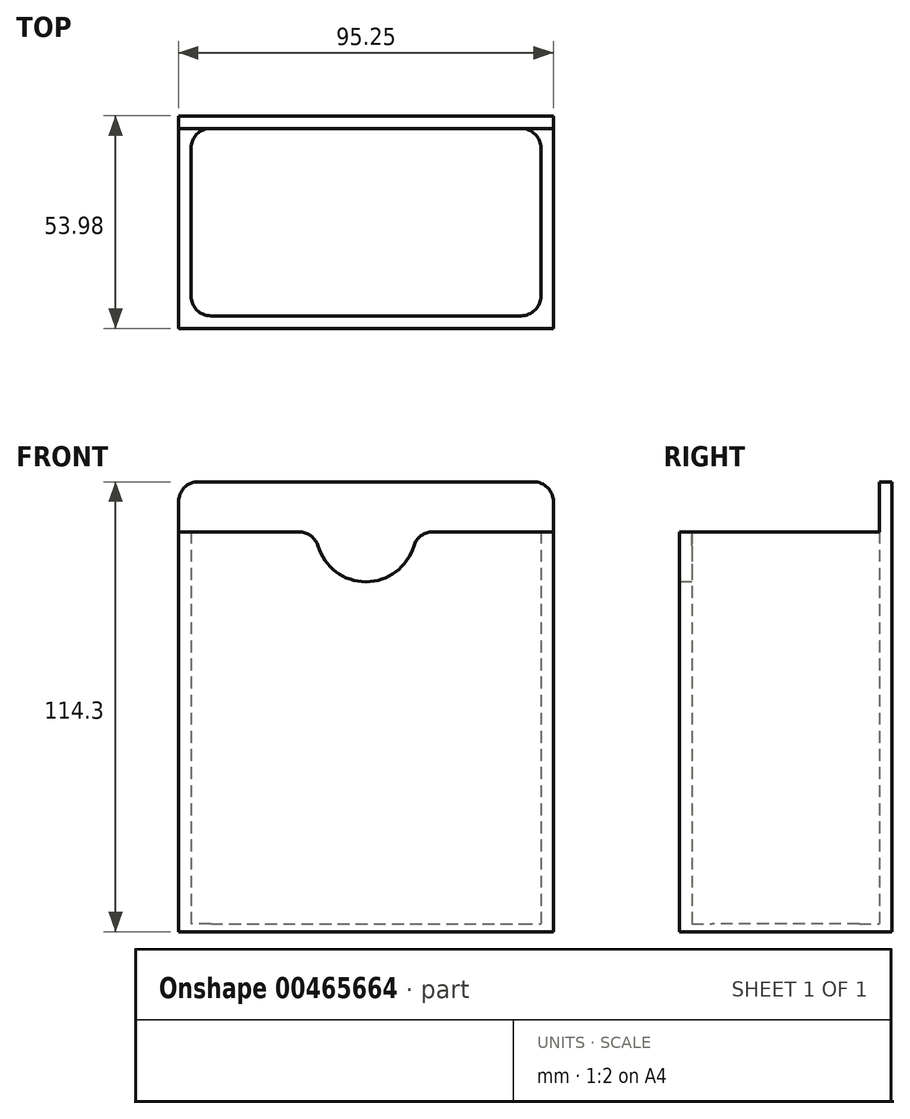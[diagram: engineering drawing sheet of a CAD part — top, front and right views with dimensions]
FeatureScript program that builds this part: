
annotation { "Feature Type Name" : "Feature", "Feature Type Description" : "" }
export const myFeature = defineFeature(function(context is Context, id is Id, definition is map)
    precondition{}
    {
        {
            var Q0;
            Q0=qCreatedBy(makeId("Top.planeOp"),FACE);
            var sketch = newSketch(context, id + "F0", { "sketchPlane" : qUnion([Q0])});
            skLineSegment(sketch, "E0.bottom", {"start": v(0, 0) * mm, "end": v(95.25, 0) * mm});
            skLineSegment(sketch, "E0.top", {"start": v(0, 53.98) * mm, "end": v(95.25, 53.98) * mm});
            skLineSegment(sketch, "E0.left", {"start": v(0, 0) * mm, "end": v(0, 53.98) * mm});
            skLineSegment(sketch, "E0.right", {"start": v(95.25, 0) * mm, "end": v(95.25, 53.98) * mm});
            skSolve(sketch);
        }
        {
            var Q0;
            Q0=qSketchRegion(id+"F0",true);
            extrude(context, id + "F1", {"entities" : qUnion([Q0]), "depth" : 2.03 * mm});
        }
        {
            var Q0;
            Q0=makeQuery(id+"F1.opExtrude","CAP_FACE",FACE,{"disambiguationData":[OSD([sQuery(id+"F0.wireOp",EDGE,"E0.bottom"),sQuery(id+"F0.wireOp",EDGE,"E0.top"),sQuery(id+"F0.wireOp",EDGE,"E0.left"),sQuery(id+"F0.wireOp",EDGE,"E0.right")])],"isStart":false});
            var sketch = newSketch(context, id + "F2", { "sketchPlane" : qUnion([Q0])});
            skLineSegment(sketch, "E1.bottom", {"start": v(0, 53.98) * mm, "end": v(95.25, 53.98) * mm});
            skLineSegment(sketch, "E1.top", {"start": v(0, 0) * mm, "end": v(95.25, 0) * mm});
            skLineSegment(sketch, "E1.left", {"start": v(0, 53.98) * mm, "end": v(0, 0) * mm});
            skLineSegment(sketch, "E1.right", {"start": v(95.25, 53.98) * mm, "end": v(95.25, 0) * mm});
            skLineSegment(sketch, "E2.0", {"start": v(3.18, 50.8) * mm, "end": v(3.18, 3.18) * mm});
            skLineSegment(sketch, "E2.1", {"start": v(3.18, 50.8) * mm, "end": v(92.08, 50.8) * mm});
            skLineSegment(sketch, "E2.2", {"start": v(92.08, 50.8) * mm, "end": v(92.08, 3.18) * mm});
            skLineSegment(sketch, "E2.3", {"start": v(3.18, 3.18) * mm, "end": v(92.08, 3.18) * mm});
            skSolve(sketch);
        }
        {
            var Q0;
            Q0=qSketchRegion(id+"F2",true);
            extrude(context, id + "F3", {"entities" : qUnion([Q0]), "operationType" : NewBodyOperationType.ADD, "depth" : 99.57 * mm});
        }
        {
            var Q0;
            Q0=makeQuery(id+"F3.opExtrude","CAP_FACE",FACE,{"disambiguationData":[OSD([sQuery(id+"F2.wireOp",EDGE,"E1.bottom"),sQuery(id+"F2.wireOp",EDGE,"E1.top"),sQuery(id+"F2.wireOp",EDGE,"E1.left"),sQuery(id+"F2.wireOp",EDGE,"E1.right"),sQuery(id+"F2.wireOp",EDGE,"E2.0"),sQuery(id+"F2.wireOp",EDGE,"E2.1"),sQuery(id+"F2.wireOp",EDGE,"E2.2"),sQuery(id+"F2.wireOp",EDGE,"E2.3")])],"isStart":false});
            var sketch = newSketch(context, id + "F4", { "sketchPlane" : qUnion([Q0])});
            skLineSegment(sketch, "E3.bottom", {"start": v(0, 53.98) * mm, "end": v(95.25, 53.98) * mm});
            skLineSegment(sketch, "E3.top", {"start": v(0, 50.8) * mm, "end": v(95.25, 50.8) * mm});
            skLineSegment(sketch, "E3.left", {"start": v(0, 53.98) * mm, "end": v(0, 50.8) * mm});
            skLineSegment(sketch, "E3.right", {"start": v(95.25, 53.98) * mm, "end": v(95.25, 50.8) * mm});
            skSolve(sketch);
        }
        {
            var Q0;
            Q0=qSketchRegion(id+"F4",true);
            extrude(context, id + "F5", {"entities" : qUnion([Q0]), "operationType" : NewBodyOperationType.ADD, "depth" : 12.7 * mm});
        }
        {
            var Q0;
            Q0=makeQuery(id+"F5.opExtrude","CAP_EDGE",EDGE,{"disambiguationData":[OSD([sQuery(id+"F4.wireOp",EDGE,"E3.left")])],"isStart":false});
            var Q1;
            Q1=makeQuery(id+"F5.opExtrude","CAP_EDGE",EDGE,{"disambiguationData":[OSD([sQuery(id+"F4.wireOp",EDGE,"E3.right")])],"isStart":false});
            fillet(context, id + "F6", {"entities" : qUnion([Q0, Q1]), "radius" : 5.08 * mm, "tangentPropagation" : true, "allowEdgeOverflow" : false});
        }
        {
            var Q0;
            Q0=makeQuery(id+"F3.opExtrude","SWEPT_EDGE",EDGE,{"disambiguationData":[OSD([sQuery(id+"F2.wireOp",EDGE,"E2.1"),sQuery(id+"F2.wireOp",EDGE,"E2.2")])]});
            var Q1;
            Q1=makeQuery(id+"F3.opExtrude","SWEPT_EDGE",EDGE,{"disambiguationData":[OSD([sQuery(id+"F2.wireOp",EDGE,"E2.0"),sQuery(id+"F2.wireOp",EDGE,"E2.1")])]});
            var Q2;
            Q2=makeQuery(id+"F3.opExtrude","SWEPT_EDGE",EDGE,{"disambiguationData":[OSD([sQuery(id+"F2.wireOp",EDGE,"E2.0"),sQuery(id+"F2.wireOp",EDGE,"E2.3")])]});
            var Q3;
            Q3=makeQuery(id+"F3.opExtrude","SWEPT_EDGE",EDGE,{"disambiguationData":[OSD([sQuery(id+"F2.wireOp",EDGE,"E2.2"),sQuery(id+"F2.wireOp",EDGE,"E2.3")])]});
            fillet(context, id + "F7", {"entities" : qUnion([Q0, Q1, Q2, Q3]), "radius" : 5.08 * mm, "tangentPropagation" : true, "allowEdgeOverflow" : false});
        }
        {
            var Q0;
            Q0=makeQuery(id+"F3.boolean.opBoolean","MERGE",FACE,{"derivedFrom":[makeQuery(id+"F1.opExtrude","SWEPT_FACE",FACE,{"disambiguationData":[OSD([sQuery(id+"F0.wireOp",EDGE,"E0.bottom")])]}),makeQuery(id+"F3.opExtrude","SWEPT_FACE",FACE,{"disambiguationData":[OSD([sQuery(id+"F2.wireOp",EDGE,"E1.top")])]})]});
            var sketch = newSketch(context, id + "F8", { "sketchPlane" : qUnion([Q0])});
            skCircle(sketch, "E4", {"center": v(47.63, 101.6) * mm, "radius": 12.7 * mm});
            skSolve(sketch);
        }
        {
            var Q0;
            Q0=qSketchRegion(id+"F8",true);
            extrude(context, id + "F9", {"entities" : qUnion([Q0]), "operationType" : NewBodyOperationType.REMOVE, "oppositeDirection" : true, "depth" : 6.35 * mm});
        }
        {
            var Q0;
            Q0=makeQuery(id+"F9.boolean.opBoolean","INTERSECT",EDGE,{"disambiguationData":[OD(0.0)],"derivedFrom":[makeQuery(id+"F3.opExtrude","CAP_FACE",FACE,{"disambiguationData":[OSD([sQuery(id+"F2.wireOp",EDGE,"E1.bottom"),sQuery(id+"F2.wireOp",EDGE,"E1.top"),sQuery(id+"F2.wireOp",EDGE,"E1.left"),sQuery(id+"F2.wireOp",EDGE,"E1.right"),sQuery(id+"F2.wireOp",EDGE,"E2.0"),sQuery(id+"F2.wireOp",EDGE,"E2.1"),sQuery(id+"F2.wireOp",EDGE,"E2.2"),sQuery(id+"F2.wireOp",EDGE,"E2.3")])],"isStart":false}),makeQuery(id+"F9.opExtrude","SWEPT_FACE",FACE,{"disambiguationData":[OSD([sQuery(id+"F8.wireOp",EDGE,"E4")])]})]});
            var Q1;
            Q1=makeQuery(id+"F9.boolean.opBoolean","INTERSECT",EDGE,{"disambiguationData":[OD(1.0)],"derivedFrom":[makeQuery(id+"F3.opExtrude","CAP_FACE",FACE,{"disambiguationData":[OSD([sQuery(id+"F2.wireOp",EDGE,"E1.bottom"),sQuery(id+"F2.wireOp",EDGE,"E1.top"),sQuery(id+"F2.wireOp",EDGE,"E1.left"),sQuery(id+"F2.wireOp",EDGE,"E1.right"),sQuery(id+"F2.wireOp",EDGE,"E2.0"),sQuery(id+"F2.wireOp",EDGE,"E2.1"),sQuery(id+"F2.wireOp",EDGE,"E2.2"),sQuery(id+"F2.wireOp",EDGE,"E2.3")])],"isStart":false}),makeQuery(id+"F9.opExtrude","SWEPT_FACE",FACE,{"disambiguationData":[OSD([sQuery(id+"F8.wireOp",EDGE,"E4")])]})]});
            fillet(context, id + "F10", {"entities" : qUnion([Q0, Q1]), "radius" : 5.08 * mm, "tangentPropagation" : true, "allowEdgeOverflow" : false});
        }
    });
